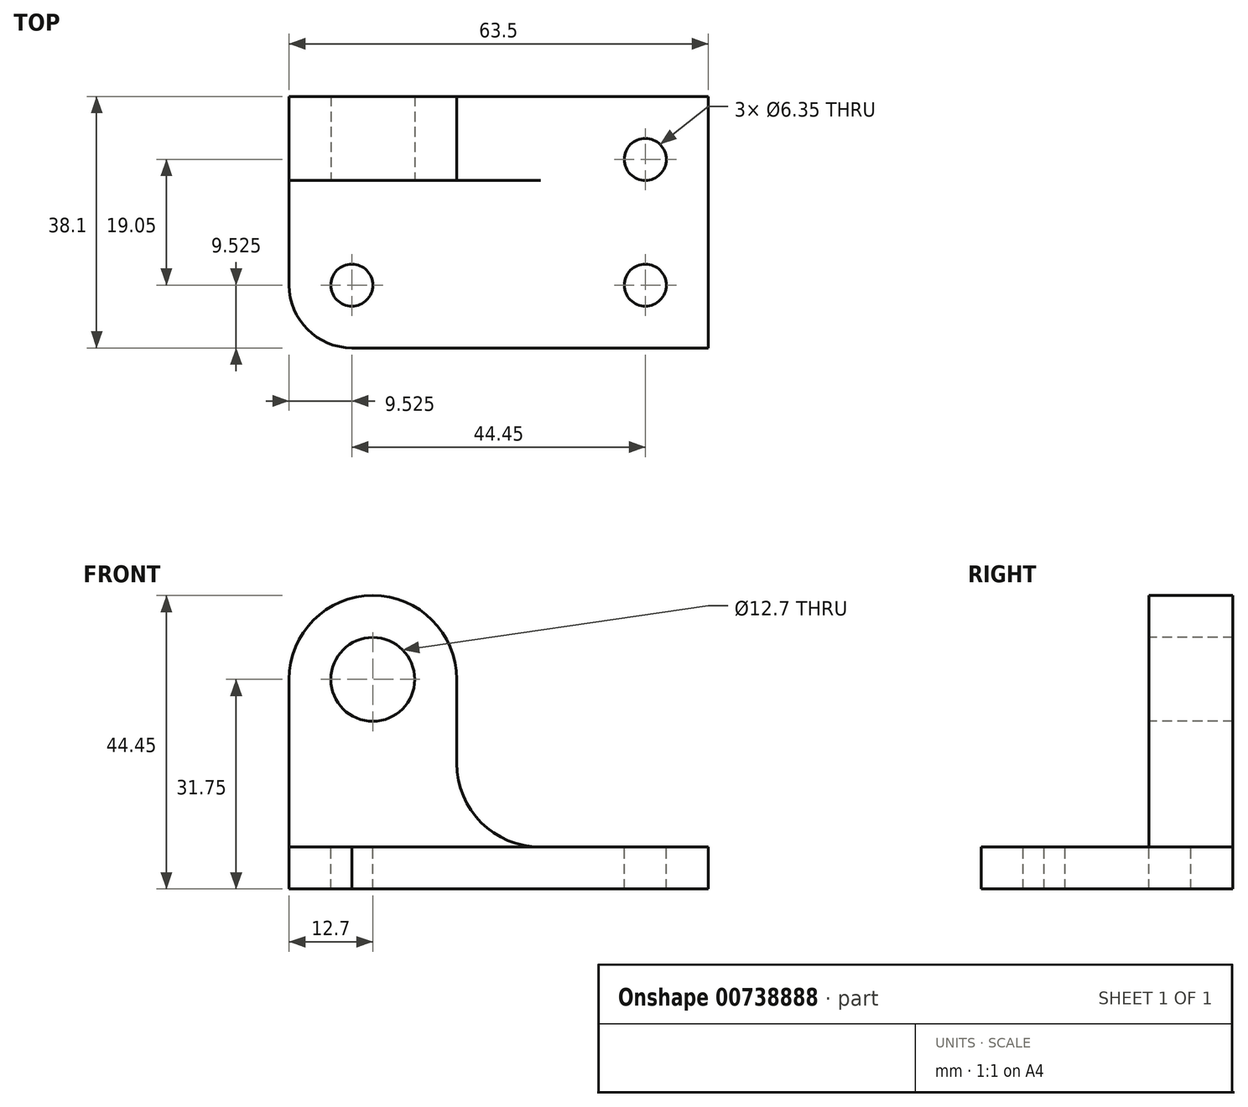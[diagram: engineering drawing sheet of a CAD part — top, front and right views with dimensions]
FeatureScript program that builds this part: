
annotation { "Feature Type Name" : "Feature", "Feature Type Description" : "" }
export const myFeature = defineFeature(function(context is Context, id is Id, definition is map)
    precondition{}
    {
        {
            var Q0;
            Q0=qCreatedBy(makeId("Front.planeOp"),FACE);
            var sketch = newSketch(context, id + "F0", { "sketchPlane" : qUnion([Q0])});
            skLineSegment(sketch, "E0", {"start": v(0, 44.45) * mm, "end": v(0, 0) * mm});
            skLineSegment(sketch, "E1", {"start": v(0, 0) * mm, "end": v(63.5, 0) * mm});
            skLineSegment(sketch, "E2", {"start": v(63.5, 0) * mm, "end": v(63.5, 44.45) * mm});
            skLineSegment(sketch, "E3", {"start": v(63.5, 44.45) * mm, "end": v(0, 44.45) * mm});
            skSolve(sketch);
        }
        {
            var Q0;
            Q0 = qSketchRegion(id + "F0", true);
            var Q1;
            {var subQ5=makeQuery(id+"F0.imprint","IMPRINT",EDGE,{"derivedFrom":sQuery(id+"F0.wireOp",EDGE,"E2")});Q1=makeQuery(id+"FgZrwNRpCxAECsg_0.imprint","IMPRINT",FACE,{"disambiguationData":[TD([[makeQuery(id+"FgZrwNRpCxAECsg_0.imprint","IMPRINT",EDGE,{"derivedFrom":subQ5}),1.0]])]});}
            extrude(context, id + "F1", {"entities" : qUnion([Q0, Q1]), "depth" : 38.1 * mm, "offsetDistance" : 25.4 * mm});
        }
        {
            var Q0;
            Q0=makeQuery(id+"F1.opExtrude","CAP_FACE",FACE,{"disambiguationData":[OSD([sQuery(id+"F0.wireOp",EDGE,"E0"),sQuery(id+"F0.wireOp",EDGE,"E1"),sQuery(id+"F0.wireOp",EDGE,"E2"),sQuery(id+"F0.wireOp",EDGE,"E3")])],"isStart":false});
            var sketch = newSketch(context, id + "F2", { "sketchPlane" : qUnion([Q0])});
            skLineSegment(sketch, "E4", {"start": v(38.1, 44.45) * mm, "end": v(38.1, 0) * mm});
            skLineSegment(sketch, "E5", {"start": v(38.1, 6.35) * mm, "end": v(63.5, 6.35) * mm});
            skSolve(sketch);
        }
        {
            var Q0;
            Q0 = qSketchRegion(id + "F2", true);
            var Q1;
            {var subQ3=sQuery(id+"F2.wireOp",EDGE,"E5");Q1=makeQuery(id+"F2.imprint","IMPRINT",FACE,{"disambiguationData":[TD([[makeQuery(id+"F2.imprint","IMPRINT",EDGE,{"derivedFrom":subQ3}),1.0]])]});}
            extrude(context, id + "F3", {"entities" : qUnion([Q0, Q1]), "operationType" : NewBodyOperationType.REMOVE, "endBound" : BoundingType.THROUGH_ALL, "oppositeDirection" : true, "depth" : 25.4 * mm, "offsetDistance" : 25.4 * mm});
        }
        {
            var Q0;
            Q0=makeQuery(id+"F1.opExtrude","CAP_FACE",FACE,{"disambiguationData":[OSD([sQuery(id+"F0.wireOp",EDGE,"E0"),sQuery(id+"F0.wireOp",EDGE,"E1"),sQuery(id+"F0.wireOp",EDGE,"E2"),sQuery(id+"F0.wireOp",EDGE,"E3")])],"isStart":false});
            var sketch = newSketch(context, id + "F4", { "sketchPlane" : qUnion([Q0])});
            skLineSegment(sketch, "E6", {"start": v(25.4, 44.45) * mm, "end": v(25.4, 0) * mm});
            skLineSegment(sketch, "E7", {"start": v(38.1, 6.35) * mm, "end": v(25.4, 6.35) * mm});
            skLineSegment(sketch, "E8", {"start": v(25.4, 19.05) * mm, "end": v(38.1, 19.05) * mm});
            skArc(sketch, "E9", {"start": v(25.4, 19.05) * mm, "mid": v(29.12, 10.07) * mm, "end": v(38.1, 6.35) * mm});
            skSolve(sketch);
        }
        {
            var Q0;
            Q0=makeQuery(id+"F3.boolean.opBoolean","COPY",FACE,{"derivedFrom":makeQuery(id+"F3.opExtrude","SWEPT_FACE",FACE,{"disambiguationData":[OSD([sQuery(id+"F2.wireOp",EDGE,"E4")])]})});
            var sketch = newSketch(context, id + "F5", { "sketchPlane" : qUnion([Q0])});
            skLineSegment(sketch, "E10", {"start": v(-12.7, 44.45) * mm, "end": v(-12.7, 6.35) * mm});
            skSolve(sketch);
        }
        {
            var Q0;
            {var subQ0=sQuery(id+"F5.wireOp",EDGE,"E10");Q0=makeQuery(id+"F5.imprint","IMPRINT",FACE,{"disambiguationData":[TD([[makeQuery(id+"F5.imprint","IMPRINT",EDGE,{"derivedFrom":subQ0}),-1.0]])]});}
            extrude(context, id + "F6", {"entities" : qUnion([Q0]), "operationType" : NewBodyOperationType.REMOVE, "endBound" : BoundingType.THROUGH_ALL, "oppositeDirection" : true, "depth" : 25.4 * mm, "offsetDistance" : 25.4 * mm});
        }
        {
            var Q0;
            {var subQ3=sQuery(id+"F4.wireOp",EDGE,"E8");Q0=makeQuery(id+"F4.imprint","IMPRINT",FACE,{"disambiguationData":[TD([[makeQuery(id+"F4.imprint","IMPRINT",EDGE,{"derivedFrom":subQ3}),1.0]])]});}
            var Q1;
            {var subQ0=sQuery(id+"F4.wireOp",EDGE,"E8");Q1=makeQuery(id+"F4.imprint","IMPRINT",FACE,{"disambiguationData":[TD([[makeQuery(id+"F4.imprint","IMPRINT",EDGE,{"derivedFrom":subQ0}),-1.0]])]});}
            extrude(context, id + "F7", {"entities" : qUnion([Q0, Q1]), "operationType" : NewBodyOperationType.REMOVE, "endBound" : BoundingType.THROUGH_ALL, "oppositeDirection" : true, "depth" : 25.4 * mm, "offsetDistance" : 25.4 * mm});
        }
        {
            var Q0;
            Q0=makeQuery(id+"F6.boolean.opBoolean","COPY",FACE,{"derivedFrom":makeQuery(id+"F6.opExtrude","SWEPT_FACE",FACE,{"disambiguationData":[OSD([sQuery(id+"F5.wireOp",EDGE,"E10")])]})});
            var sketch = newSketch(context, id + "F8", { "sketchPlane" : qUnion([Q0])});
            skCircle(sketch, "E11", {"center": v(12.7, 31.75) * mm, "radius": 6.35 * mm});
            skArc(sketch, "E12", {"start": v(25.4, 31.75) * mm, "mid": v(12.7, 44.45) * mm, "end": v(0, 31.75) * mm});
            skSolve(sketch);
        }
        {
            var Q0;
            Q0 = qSketchRegion(id + "F8", true);
            var Q1;
            {var subQ0=sQuery(id+"F8.wireOp",EDGE,"E12");var subQ1=sQuery(id+"F5.wireOp",EDGE,"E10");var subQ2=makeQuery(id+"F7.boolean.opBoolean","INTERSECT",EDGE,{"derivedFrom":[makeQuery(id+"F6.boolean.opBoolean","COPY",FACE,{"derivedFrom":makeQuery(id+"F6.opExtrude","SWEPT_FACE",FACE,{"disambiguationData":[OSD([subQ1])]})}),makeQuery(id+"F7.opExtrude","SWEPT_FACE",FACE,{"disambiguationData":[OSD([sQuery(id+"F4.wireOp",EDGE,"E6")])]})]});var subQ3=makeQuery(id+"F8.imprint","INTERSECT",VERTEX,{"derivedFrom":[subQ2,subQ0]});Q1=makeQuery(id+"F8.imprint","IMPRINT",FACE,{"disambiguationData":[TD([[makeQuery(id+"F8.imprint","IMPRINT",EDGE,{"disambiguationData":[TD([[subQ3,-1.0]])],"derivedFrom":subQ0}),-1.0]])]});}
            var Q2;
            {var subQ0=sQuery(id+"F8.wireOp",EDGE,"E12");var subQ1=sQuery(id+"F5.wireOp",EDGE,"E10");var subQ2=makeQuery(id+"F6.boolean.opBoolean","INTERSECT",EDGE,{"derivedFrom":[makeQuery(id+"F1.opExtrude","SWEPT_FACE",FACE,{"disambiguationData":[OSD([sQuery(id+"F0.wireOp",EDGE,"E0")])]}),makeQuery(id+"F6.opExtrude","SWEPT_FACE",FACE,{"disambiguationData":[OSD([subQ1])]})]});var subQ3=makeQuery(id+"F8.imprint","INTERSECT",VERTEX,{"derivedFrom":[subQ2,subQ0]});Q2=makeQuery(id+"F8.imprint","IMPRINT",FACE,{"disambiguationData":[TD([[makeQuery(id+"F8.imprint","IMPRINT",EDGE,{"disambiguationData":[TD([[subQ3,1.0]])],"derivedFrom":subQ0}),-1.0]])]});}
            extrude(context, id + "F9", {"entities" : qUnion([Q0, Q1, Q2]), "operationType" : NewBodyOperationType.REMOVE, "endBound" : BoundingType.THROUGH_ALL, "oppositeDirection" : true, "depth" : 25.4 * mm, "offsetDistance" : 25.4 * mm});
        }
        {
            var Q0;
            {var subQ0=sQuery(id+"F2.wireOp",EDGE,"E5");Q0=makeQuery(id+"F6.boolean.opBoolean","MERGE",FACE,{"derivedFrom":[makeQuery(id+"F3.boolean.opBoolean","COPY",FACE,{"derivedFrom":makeQuery(id+"F3.opExtrude","SWEPT_FACE",FACE,{"disambiguationData":[OSD([subQ0])]})}),makeQuery(id+"F6.opExtrude","SWEPT_FACE",FACE,{"disambiguationData":[OSD([sQuery(id+"F2.wireOp",EDGE,"E4"),subQ0])]})]});}
            var sketch = newSketch(context, id + "F10", { "sketchPlane" : qUnion([Q0])});
            skCircle(sketch, "E13", {"center": v(9.53, -28.58) * mm, "radius": 3.18 * mm});
            skCircle(sketch, "E14", {"center": v(53.97, -9.52) * mm, "radius": 3.18 * mm});
            skCircle(sketch, "E15", {"center": v(53.97, -28.57) * mm, "radius": 3.18 * mm});
            skArc(sketch, "E16", {"start": v(0, -28.57) * mm, "mid": v(2.82, -35.28) * mm, "end": v(9.52, -38.1) * mm});
            skArc(sketch, "E17", {"start": v(53.97, -38.1) * mm, "mid": v(60.96, -35.56) * mm, "end": v(63.5, -28.57) * mm});
            skArc(sketch, "E18", {"start": v(63.5, -9.52) * mm, "mid": v(60.6, -2.37) * mm, "end": v(53.25, 0) * mm});
            skSolve(sketch);
        }
        {
            var Q0;
            {var subQ0=sQuery(id+"F10.wireOp",EDGE,"E18");var subQ1=sQuery(id+"F2.wireOp",EDGE,"E5");var subQ2=sQuery(id+"F0.wireOp",EDGE,"E2");var subQ3=makeQuery(id+"F3.boolean.opBoolean","COPY",EDGE,{"derivedFrom":makeQuery(id+"F3.opExtrude","SWEPT_EDGE",EDGE,{"disambiguationData":[OSD([subQ2,subQ1])]})});var subQ4=makeQuery(id+"F10.imprint","INTERSECT",VERTEX,{"disambiguationData":[OD(1.0)],"derivedFrom":[subQ3,subQ0]});Q0=makeQuery(id+"F10.imprint","IMPRINT",FACE,{"disambiguationData":[TD([[makeQuery(id+"F10.imprint","IMPRINT",EDGE,{"disambiguationData":[TD([[subQ4,-1.0]])],"derivedFrom":subQ0}),-1.0]])]});}
            var Q1;
            {var subQ0=sQuery(id+"F10.wireOp",EDGE,"E17");var subQ1=sQuery(id+"F2.wireOp",EDGE,"E5");var subQ4=makeQuery(id+"F3.boolean.opBoolean","COPY",EDGE,{"derivedFrom":makeQuery(id+"F3.opExtrude","SWEPT_EDGE",EDGE,{"disambiguationData":[OSD([sQuery(id+"F0.wireOp",EDGE,"E2"),subQ1])]})});var subQ5=makeQuery(id+"F10.imprint","INTERSECT",VERTEX,{"disambiguationData":[OD(1.0)],"derivedFrom":[subQ4,subQ0]});Q1=makeQuery(id+"F10.imprint","IMPRINT",FACE,{"disambiguationData":[TD([[makeQuery(id+"F10.imprint","IMPRINT",EDGE,{"disambiguationData":[TD([[subQ5,1.0]])],"derivedFrom":subQ0}),-1.0]])]});}
            var Q2;
            {var subQ0=sQuery(id+"F10.wireOp",EDGE,"E16");Q2=makeQuery(id+"F10.imprint","IMPRINT",FACE,{"disambiguationData":[TD([[makeQuery(id+"F10.imprint","IMPRINT",EDGE,{"derivedFrom":subQ0}),-1.0]])]});}
            var Q3;
            Q3=makeQuery(id+"F10.imprint","IMPRINT",FACE,{"disambiguationData":[TD([[makeQuery(id+"F10.imprint","IMPRINT",EDGE,{"derivedFrom":sQuery(id+"F10.wireOp",EDGE,"E13")}),1.0]])]});
            var Q4;
            Q4=makeQuery(id+"F10.imprint","IMPRINT",FACE,{"disambiguationData":[TD([[makeQuery(id+"F10.imprint","IMPRINT",EDGE,{"derivedFrom":sQuery(id+"F10.wireOp",EDGE,"E15")}),1.0]])]});
            var Q5;
            Q5=makeQuery(id+"F10.imprint","IMPRINT",FACE,{"disambiguationData":[TD([[makeQuery(id+"F10.imprint","IMPRINT",EDGE,{"derivedFrom":sQuery(id+"F10.wireOp",EDGE,"E14")}),1.0]])]});
            extrude(context, id + "F11", {"entities" : qUnion([Q0, Q1, Q2, Q3, Q4, Q5]), "operationType" : NewBodyOperationType.REMOVE, "endBound" : BoundingType.THROUGH_ALL, "oppositeDirection" : true, "depth" : 25.4 * mm, "offsetDistance" : 25.4 * mm});
        }
    });
